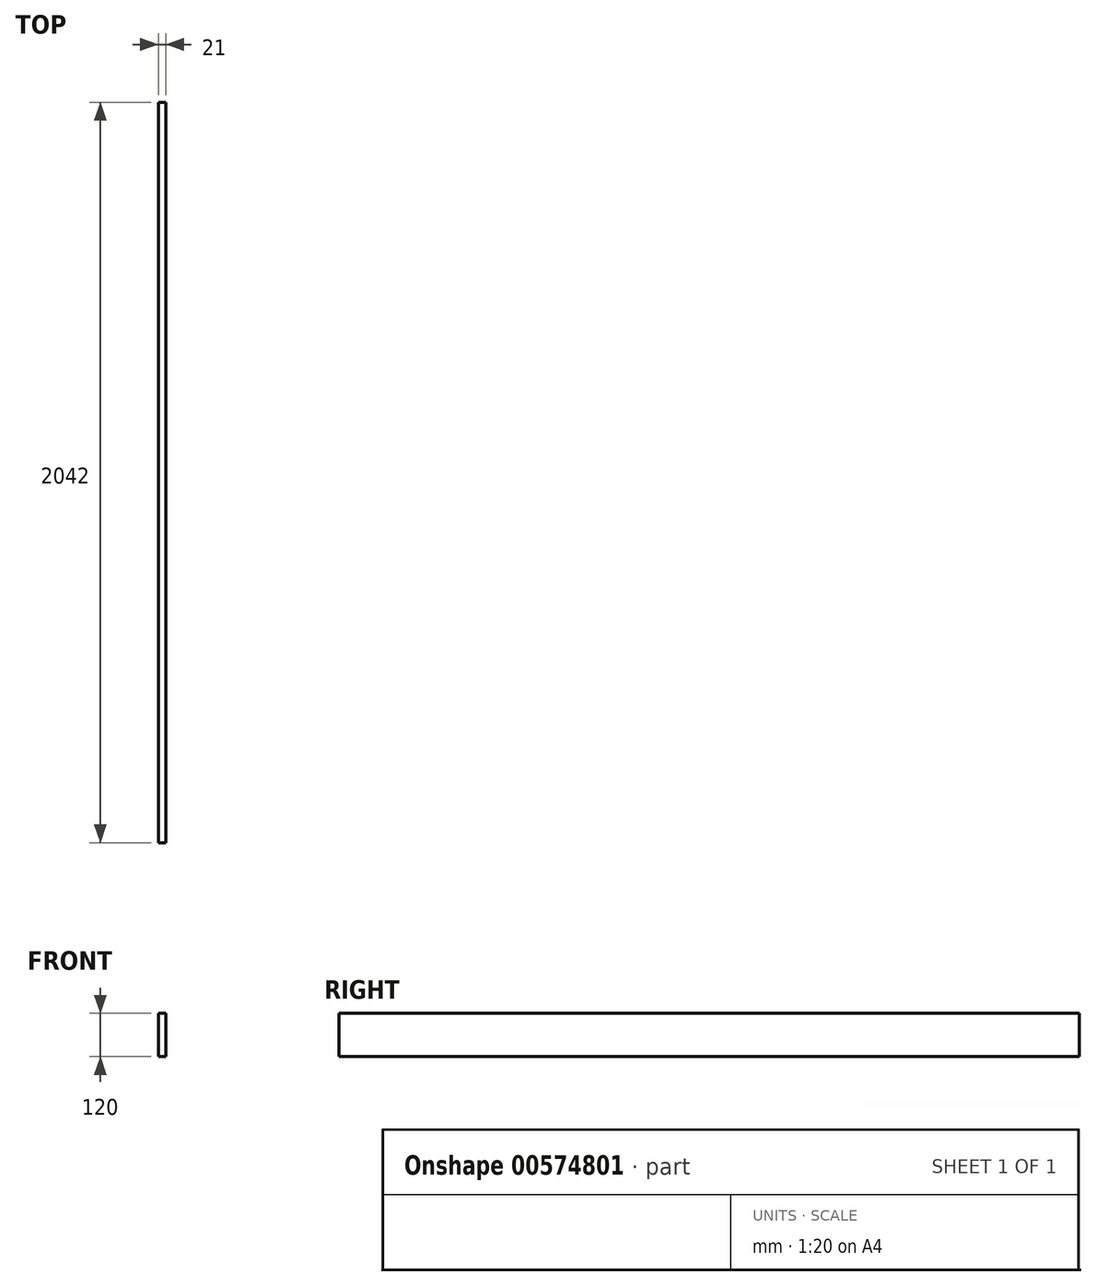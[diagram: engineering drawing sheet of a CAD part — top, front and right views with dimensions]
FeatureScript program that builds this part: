
annotation { "Feature Type Name" : "Feature", "Feature Type Description" : "" }
export const myFeature = defineFeature(function(context is Context, id is Id, definition is map)
    precondition{}
    {
        {
            var Q0;
            Q0=qCreatedBy(makeId("Front.planeOp"),FACE);
            var sketch = newSketch(context, id + "F0", { "sketchPlane" : qUnion([Q0])});
            skLineSegment(sketch, "E0.bottom", {"start": v(-10.5, 60) * mm, "end": v(10.5, 60) * mm});
            skLineSegment(sketch, "E0.top", {"start": v(-10.5, -60) * mm, "end": v(10.5, -60) * mm});
            skLineSegment(sketch, "E0.left", {"start": v(-10.5, 60) * mm, "end": v(-10.5, -60) * mm});
            skLineSegment(sketch, "E0.right", {"start": v(10.5, 60) * mm, "end": v(10.5, -60) * mm});
            skSolve(sketch);
        }
        {
            var Q0;
            Q0 = qSketchRegion(id + "F0", true);
            extrude(context, id + "F1", {"entities" : qUnion([Q0]), "depth" : 2042 * mm, "offsetDistance" : 25 * mm});
        }
    });
